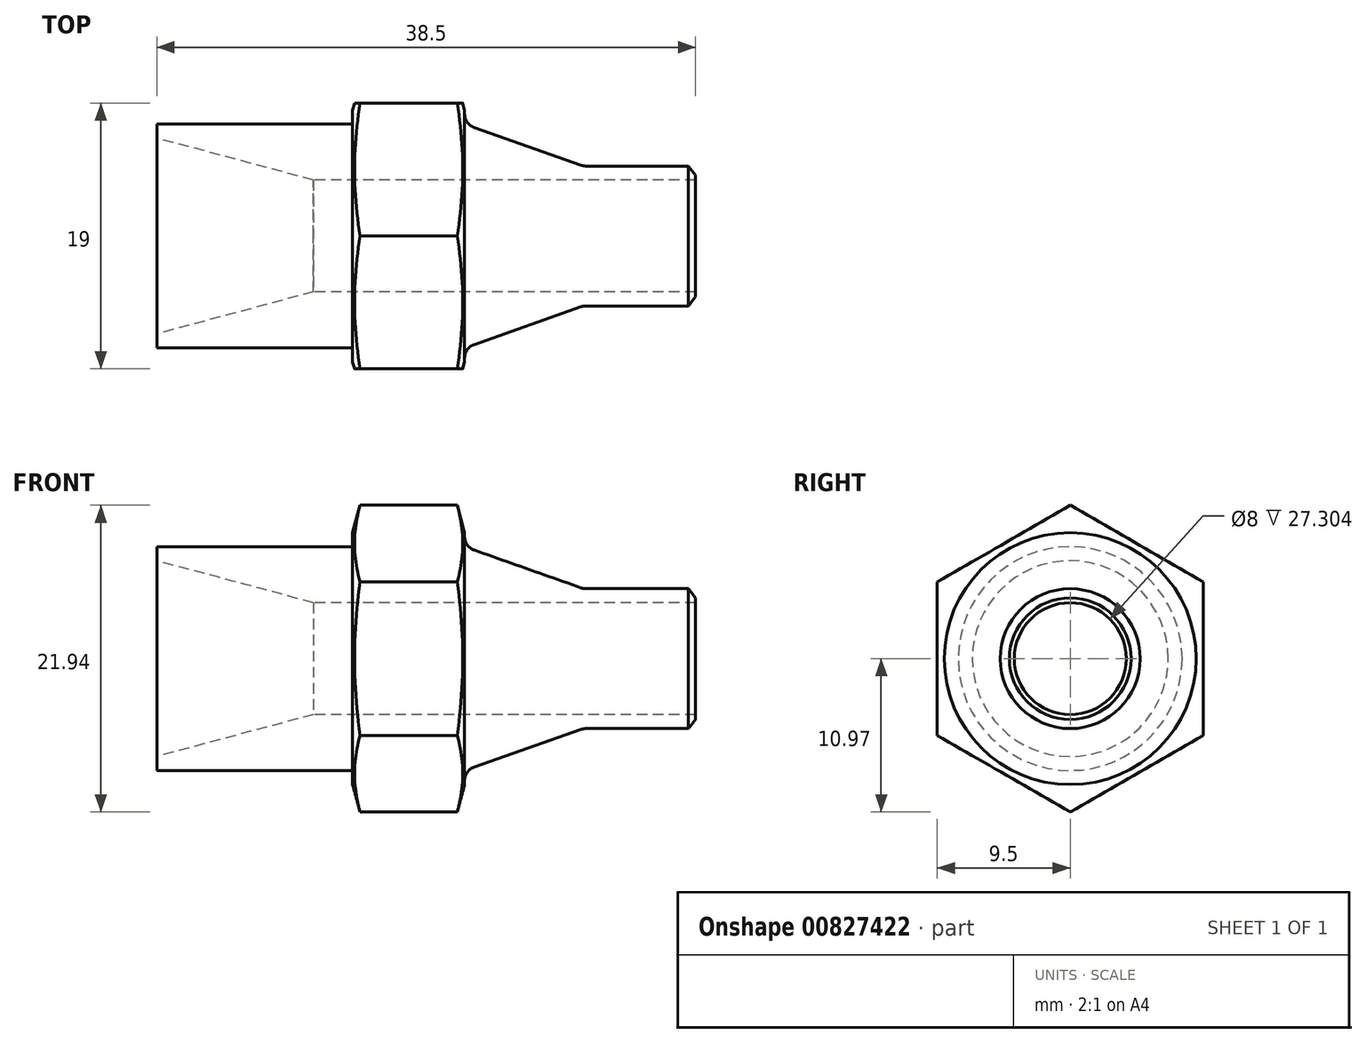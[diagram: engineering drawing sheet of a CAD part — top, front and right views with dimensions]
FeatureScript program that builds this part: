
annotation { "Feature Type Name" : "Feature", "Feature Type Description" : "" }
export const myFeature = defineFeature(function(context is Context, id is Id, definition is map)
    precondition{}
    {
        {
            var Q0;
            Q0=qCreatedBy(makeId("Front.planeOp"),FACE);
            var sketch = newSketch(context, id + "F0", { "sketchPlane" : qUnion([Q0])});
            skLineSegment(sketch, "E0", {"start": v(-9.15, 0) * mm, "end": v(9.54, 0) * mm, "construction": true});
            skLineSegment(sketch, "E1", {"start": v(0, 4) * mm, "end": v(-27.3, 4) * mm});
            skLineSegment(sketch, "E2", {"start": v(-27.3, 4) * mm, "end": v(-38.5, 7) * mm});
            skLineSegment(sketch, "E3", {"start": v(-38.5, 7) * mm, "end": v(-38.5, 8) * mm});
            skLineSegment(sketch, "E4", {"start": v(-38.5, 8) * mm, "end": v(-24.5, 8) * mm});
            skLineSegment(sketch, "E5", {"start": v(-24.5, 8) * mm, "end": v(-24.5, 12) * mm});
            skLineSegment(sketch, "E6", {"start": v(-24.5, 12) * mm, "end": v(-16.5, 12) * mm});
            skLineSegment(sketch, "E7", {"start": v(-16.5, 12) * mm, "end": v(-16.5, 8) * mm});
            skLineSegment(sketch, "E8", {"start": v(-16.5, 8) * mm, "end": v(-8, 5) * mm});
            skLineSegment(sketch, "E9", {"start": v(-8, 5) * mm, "end": v(0, 5) * mm});
            skLineSegment(sketch, "E10", {"start": v(0, 5) * mm, "end": v(0, 4) * mm});
            skLineSegment(sketch, "E11", {"start": v(-44.19, 4) * mm, "end": v(-32.5, 4) * mm, "construction": true});
            skLineSegment(sketch, "E12", {"start": v(-32.5, 4) * mm, "end": v(-32.5, 5) * mm, "construction": true});
            skLineSegment(sketch, "E13", {"start": v(-32.5, 5) * mm, "end": v(-39.96, 7) * mm, "construction": true});
            skLineSegment(sketch, "E14", {"start": v(-39.96, 7) * mm, "end": v(-39.96, 5) * mm, "construction": true});
            skLineSegment(sketch, "E15", {"start": v(-39.96, 5) * mm, "end": v(-44.19, 5) * mm, "construction": true});
            skLineSegment(sketch, "E16", {"start": v(-44.19, 5) * mm, "end": v(-44.19, 4) * mm, "construction": true});
            skArc(sketch, "E17", {"start": v(-32.5, 5) * mm, "mid": v(-36.13, 6.36) * mm, "end": v(-39.96, 7) * mm, "construction": true});
            skSolve(sketch);
        }
        {
            var Q0;
            Q0=makeQuery(id+"F0.imprint","IMPRINT",FACE,{"disambiguationData":[TD([[makeQuery(id+"F0.imprint","IMPRINT",EDGE,{"derivedFrom":sQuery(id+"F0.wireOp",EDGE,"E1")}),-1.0]])]});
            var Q1;
            Q1=sQuery(id+"F0.wireOp",EDGE,"E0");
            revolve(context, id + "F1", {"surfaceOperationType" : NewSurfaceOperationType.NEW, "entities" : qUnion([Q0]), "axis" : qUnion([Q1]), "revolveType" : RevolveType.FULL});
        }
        {
            var Q0;
            Q0=makeQuery(id+"F1.opRevolve","SWEPT_EDGE",EDGE,{"disambiguationData":[OSD([sQuery(id+"F0.wireOp",EDGE,"E9"),sQuery(id+"F0.wireOp",EDGE,"E10")])]});
            chamfer(context, id + "F2", {"entities" : qUnion([Q0]), "chamferType" : ChamferType.OFFSET_ANGLE, "width" : .5 * mm, "oppositeDirection" : false, "angle" : 52.5 * degree, "tangentPropagation" : true});
        }
        {
            var Q0;
            Q0=makeQuery(id+"F1.opRevolve","SWEPT_EDGE",EDGE,{"disambiguationData":[OSD([sQuery(id+"F0.wireOp",EDGE,"E7"),sQuery(id+"F0.wireOp",EDGE,"E8")])]});
            var Q1;
            Q1=makeQuery(id+"F1.opRevolve","SWEPT_EDGE",EDGE,{"disambiguationData":[OSD([sQuery(id+"F0.wireOp",EDGE,"E8"),sQuery(id+"F0.wireOp",EDGE,"E9")])]});
            fillet(context, id + "F3", {"entities" : qUnion([Q0, Q1]), "radius" : 1 * mm, "tangentPropagation" : true, "allowEdgeOverflow" : false});
        }
        {
            var Q0;
            Q0=makeQuery(id+"F1.opRevolve","SWEPT_FACE",FACE,{"disambiguationData":[OSD([sQuery(id+"F0.wireOp",EDGE,"E5")])]});
            var sketch = newSketch(context, id + "F4", { "sketchPlane" : qUnion([Q0])});
            skCircle(sketch, "E18.cCircle", {"center": v(0, 0) * mm, "radius": 9.5 * mm, "construction": true});
            skLineSegment(sketch, "E18.0", {"start": v(-9.5, 5.48) * mm, "end": v(0, 10.97) * mm});
            skLineSegment(sketch, "E18.1", {"start": v(0, 10.97) * mm, "end": v(9.5, 5.48) * mm});
            skLineSegment(sketch, "E18.2", {"start": v(9.5, 5.48) * mm, "end": v(9.5, -5.48) * mm});
            skLineSegment(sketch, "E18.3", {"start": v(9.5, -5.48) * mm, "end": v(0, -10.97) * mm});
            skLineSegment(sketch, "E18.4", {"start": v(0, -10.97) * mm, "end": v(-9.5, -5.48) * mm});
            skLineSegment(sketch, "E18.5", {"start": v(-9.5, -5.48) * mm, "end": v(-9.5, 5.48) * mm});
            skPoint(sketch, "E18.0.midPoint", {"position": v(-4.75, 8.23) * mm});
            skSolve(sketch);
        }
        {
            var Q0;
            Q0=makeQuery(id+"F4.imprint","IMPRINT",FACE,{"disambiguationData":[TD([[makeQuery(id+"F4.imprint","IMPRINT",EDGE,{"derivedFrom":sQuery(id+"F4.wireOp",EDGE,"E18.0")}),1.0]])]});
            extrude(context, id + "F5", {"entities" : qUnion([Q0]), "operationType" : NewBodyOperationType.REMOVE, "oppositeDirection" : true, "depth" : 25 * mm, "offsetDistance" : 25 * mm});
        }
        {
            var Q0;
            Q0=qCreatedBy(makeId("Front.planeOp"),FACE);
            var sketch = newSketch(context, id + "F6", { "sketchPlane" : qUnion([Q0])});
            skLineSegment(sketch, "E19.0", {"start": v(-24.5, 10.97) * mm, "end": v(-24.5, 5.48) * mm});
            skLineSegment(sketch, "E20.0", {"start": v(-16.5, 5.48) * mm, "end": v(-16.5, 10.97) * mm});
            skLineSegment(sketch, "E21", {"start": v(-24.5, 9) * mm, "end": v(-23.27, 13.6) * mm});
            skLineSegment(sketch, "E22", {"start": v(-23.27, 13.6) * mm, "end": v(-24.5, 13.6) * mm});
            skLineSegment(sketch, "E23", {"start": v(-24.5, 13.6) * mm, "end": v(-24.5, 9) * mm});
            skLineSegment(sketch, "E24.0", {"start": v(-16.5, 5.48) * mm, "end": v(-24.5, 5.48) * mm});
            skLineSegment(sketch, "E25", {"start": v(-20.5, 5.48) * mm, "end": v(-20.5, 14.64) * mm, "construction": true});
            skLineSegment(sketch, "E26.MirrorCS", {"start": v(-16.5, 9) * mm, "end": v(-17.73, 13.6) * mm});
            skLineSegment(sketch, "E27.MirrorCS", {"start": v(-17.73, 13.6) * mm, "end": v(-16.5, 13.6) * mm});
            skLineSegment(sketch, "E28.MirrorCS", {"start": v(-16.5, 13.6) * mm, "end": v(-16.5, 9) * mm});
            skLineSegment(sketch, "E29", {"start": v(-43.66, 0) * mm, "end": v(53.87, 0) * mm, "construction": true});
            skSolve(sketch);
        }
        {
            var Q0;
            {var subQ0=sQuery(id+"F6.wireOp",EDGE,"E21");Q0=makeQuery(id+"F6.imprint","IMPRINT",FACE,{"disambiguationData":[TD([[makeQuery(id+"F6.imprint","IMPRINT",EDGE,{"derivedFrom":subQ0}),1.0]])]});}
            var Q1;
            {var subQ0=sQuery(id+"F6.wireOp",EDGE,"E26.MirrorCS");Q1=makeQuery(id+"F6.imprint","IMPRINT",FACE,{"disambiguationData":[TD([[makeQuery(id+"F6.imprint","IMPRINT",EDGE,{"derivedFrom":subQ0}),-1.0]])]});}
            var Q2;
            Q2=sQuery(id+"F6.wireOp",EDGE,"E29");
            revolve(context, id + "F7", {"operationType" : NewBodyOperationType.REMOVE, "surfaceOperationType" : NewSurfaceOperationType.NEW, "entities" : qUnion([Q0, Q1]), "axis" : qUnion([Q2]), "revolveType" : RevolveType.FULL, "oppositeDirection" : true});
        }
    });
